FCSTD DOCUMENT  (FreeCAD 0.19R21858 (Git))
Label: solid_v_wheel_assembly
License: All rights reserved
LicenseURL: http://en.wikipedia.org/wiki/All_rights_reserved
objects: App::Link×3, App::DocumentObjectGroup×2, PartDesign::CoordinateSystem×1, App::FeaturePython×1, App::Part×1
note: 1 computed .brp shape members not serialized (recipe doc carries the construction recipe); baked Part::Feature solids carry a one-line shape summary decoded from their .brp
EXTERNAL_REF file=625RS_bearing.FCStd obj=LCS_2
EXTERNAL_REF file=delrin_solid_v-wheel.FCStd obj=LCS_1
EXTERNAL_REF file=delrin_solid_v-wheel.FCStd obj=Part
EXTERNAL_REF file=625RS_bearing.FCStd obj=LCS_1
EXTERNAL_REF file=625RS_bearing.FCStd obj=Part
EXTERNAL_REF file=delrin_solid_v-wheel.FCStd obj=LCS_2

FEATURE [App::DocumentObjectGroup] Parts
FEATURE [PartDesign::CoordinateSystem] LCS_Origin
  AttacherType = Attacher::AttachEngine3D
  MapMode = 2
  Support = -> [X_Axis]
FEATURE [App::DocumentObjectGroup] Constraints
FEATURE [App::FeaturePython] Variables  # WARN: FeaturePython — macro-defined, semantics opaque (R4)
FEATURE [App::Link] delrin_solid_v_wheel_delrin_solid_v_wheel  label="delrin_solid_v_wheel_delrin_solid_v-wheel"
  AssemblyType = Asm4EE
  AttachedBy = #LCS_1
  AttachedTo = _25RS_bearing_625RS_bearing#LCS_2
  LinkPlacement = pos=(-4e-16,3e-16,-5.5) rot=(0.57735,-0.57735,0.57735;2.0944rad)
  LinkedObject = -> <external delrin_solid_v-wheel.FCStd>#Part
  Placement = pos=(-4e-16,3e-16,-5.5) rot=(0.57735,-0.57735,0.57735;2.0944rad)
  expr: Placement = _25RS_bearing_625RS_bearing.Placement * _25RS_bearing#LCS_2.Placement * AttachmentOffset * delrin_solid_v_wheel#LCS_1.Placement ^ -1
FEATURE [App::Link] _25RS_bearing_625RS_bearing
  AssemblyType = Asm4EE
  AttachedBy = #LCS_1
  AttachedTo = Parent Assembly#LCS_Origin
  LinkPlacement = pos=(-1e-16,1e-16,-2.5) rot=(-0.57735,-0.57735,-0.57735;2.0944rad)
  LinkedObject = -> <external 625RS_bearing.FCStd>#Part
  Placement = pos=(-1e-16,1e-16,-2.5) rot=(-0.57735,-0.57735,-0.57735;2.0944rad)
  expr: Placement = LCS_Origin.Placement * AttachmentOffset * _25RS_bearing#LCS_1.Placement ^ -1
FEATURE [App::Link] _25RS_bearing_625RS_bearing_2
  AssemblyType = Asm4EE
  AttachedBy = #LCS_2
  AttachedTo = delrin_solid_v_wheel_delrin_solid_v_wheel#LCS_2
  AttachmentOffset = pos=(0,0,0) rot=(1,0,0;3.14159rad)
  LinkPlacement = pos=(2e-16,1.4e-15,-8.5) rot=(0.57735,0.57735,-0.57735;2.0944rad)
  LinkedObject = -> <external 625RS_bearing.FCStd>#Part
  Placement = pos=(2e-16,1.4e-15,-8.5) rot=(0.57735,0.57735,-0.57735;2.0944rad)
  expr: Placement = delrin_solid_v_wheel_delrin_solid_v_wheel.Placement * delrin_solid_v_wheel#LCS_2.Placement * AttachmentOffset * _25RS_bearing#LCS_2.Placement ^ -1
FEATURE [App::Part] Model
  Configuration = 0
  Group = -> [LCS_Origin,Constraints,Variables,delrin_solid_v_wheel_delrin_solid_v_wheel,_25RS_bearing_625RS_bearing,_25RS_bearing_625RS_bearing_2]
  Origin = -> Origin
  Type = Assembly4 Model
